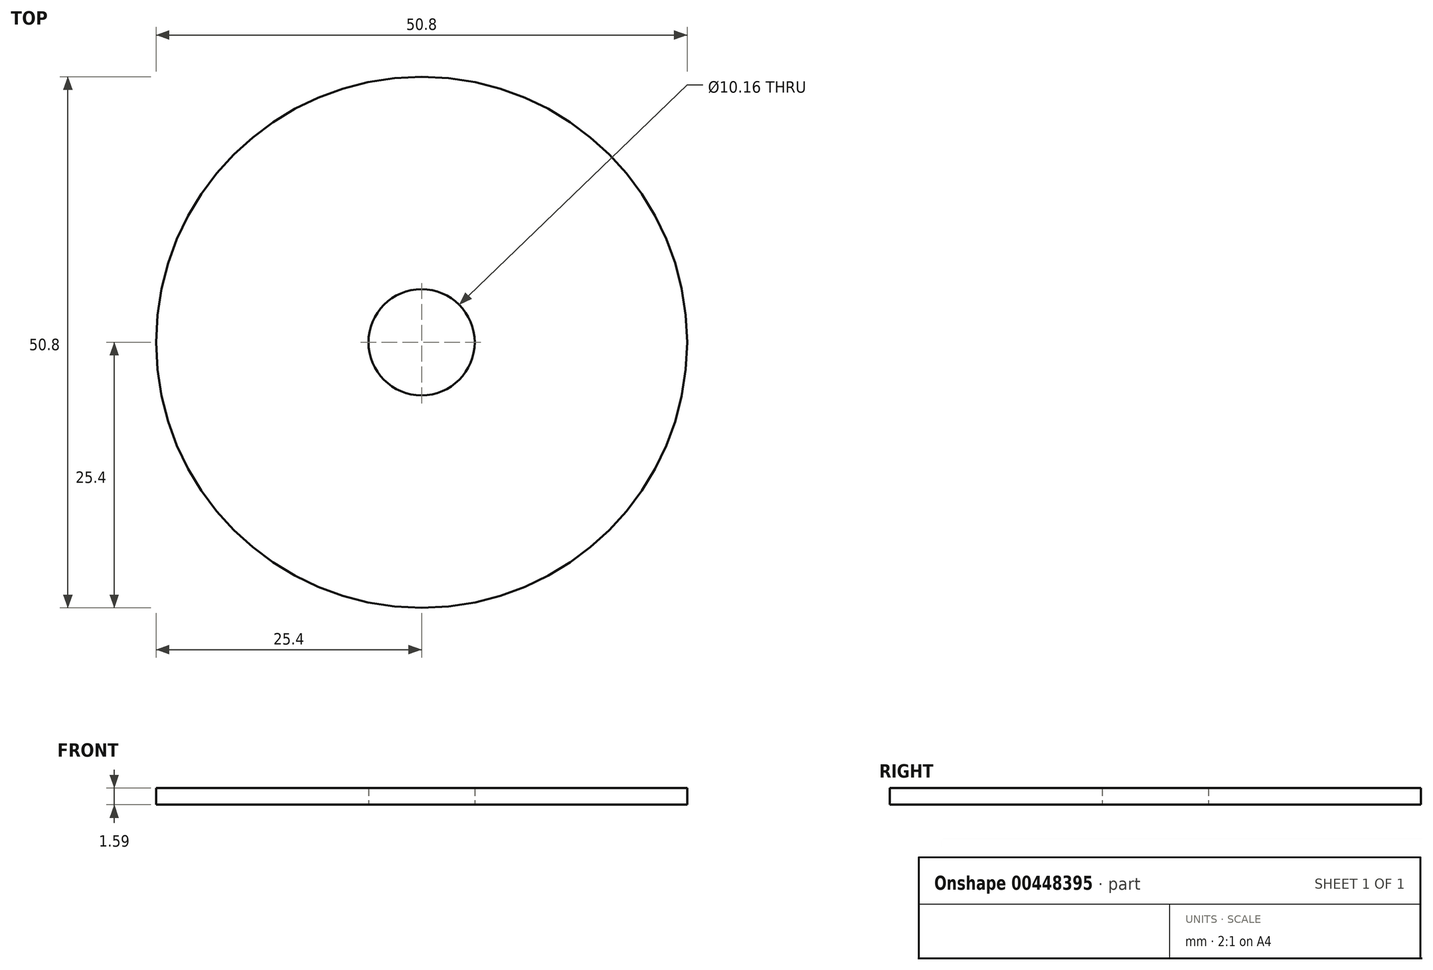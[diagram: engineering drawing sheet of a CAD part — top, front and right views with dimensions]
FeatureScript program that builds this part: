
annotation { "Feature Type Name" : "Feature", "Feature Type Description" : "" }
export const myFeature = defineFeature(function(context is Context, id is Id, definition is map)
    precondition{}
    {
        {
            var Q0;
            Q0=qCreatedBy(makeId("Top.planeOp"),FACE);
            var sketch = newSketch(context, id + "F0", { "sketchPlane" : qUnion([Q0])});
            skCircle(sketch, "E0", {"center": v(0, 0) * mm, "radius": 25.4 * mm});
            skCircle(sketch, "E1", {"center": v(0, 0) * mm, "radius": 5.08 * mm});
            skSolve(sketch);
        }
        {
            var Q0;
            Q0 = qSketchRegion(id + "F0", true);
            extrude(context, id + "F1", {"entities" : qUnion([Q0]), "depth" : 1.59 * mm, "offsetDistance" : 25.4 * mm});
        }
    });
